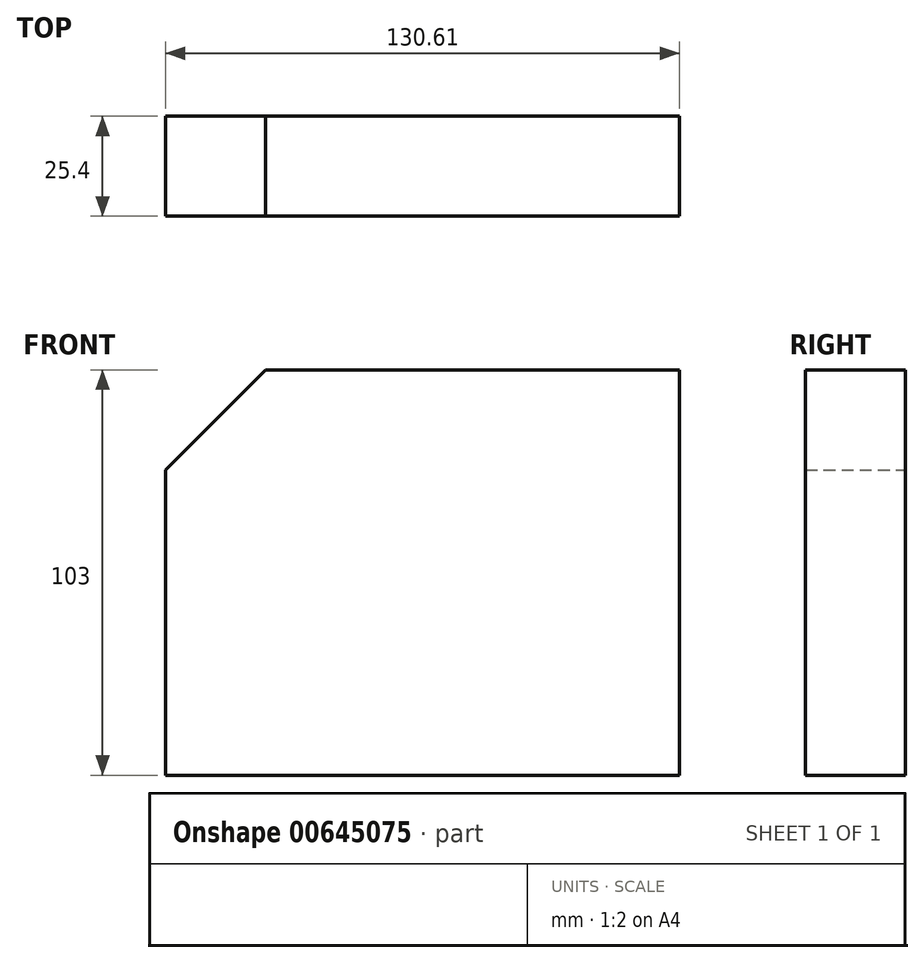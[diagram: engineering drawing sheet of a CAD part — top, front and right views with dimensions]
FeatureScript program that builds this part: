
annotation { "Feature Type Name" : "Feature", "Feature Type Description" : "" }
export const myFeature = defineFeature(function(context is Context, id is Id, definition is map)
    precondition{}
    {
        {
            var Q0;
            Q0=qCreatedBy(makeId("Front.planeOp"),FACE);
            var sketch = newSketch(context, id + "F0", { "sketchPlane" : qUnion([Q0])});
            skLineSegment(sketch, "E0.bottom", {"start": v(-91.23, 70.75) * mm, "end": v(39.38, 70.75) * mm});
            skLineSegment(sketch, "E0.top", {"start": v(-91.23, -32.25) * mm, "end": v(39.38, -32.25) * mm});
            skLineSegment(sketch, "E0.left", {"start": v(-91.23, 70.75) * mm, "end": v(-91.23, -32.25) * mm});
            skLineSegment(sketch, "E0.right", {"start": v(39.38, 70.75) * mm, "end": v(39.38, -32.25) * mm});
            skSolve(sketch);
        }
        {
            var Q0;
            Q0=makeQuery(id+"F0.imprint","IMPRINT",FACE,{"disambiguationData":[TD([[makeQuery(id+"F0.imprint","IMPRINT",EDGE,{"derivedFrom":sQuery(id+"F0.wireOp",EDGE,"E0.bottom")}),-1.0]])]});
            extrude(context, id + "F1", {"entities" : qUnion([Q0]), "depth" : 25.4 * mm, "offsetDistance" : 25.4 * mm});
        }
        {
            var Q0;
            Q0=makeQuery(id+"F1.opExtrude","SWEPT_EDGE",EDGE,{"disambiguationData":[OSD([sQuery(id+"F0.wireOp",EDGE,"E0.bottom"),sQuery(id+"F0.wireOp",EDGE,"E0.left")])]});
            chamfer(context, id + "F2", {"entities" : qUnion([Q0]), "width" : 25.4 * mm, "tangentPropagation" : true});
        }
    });
